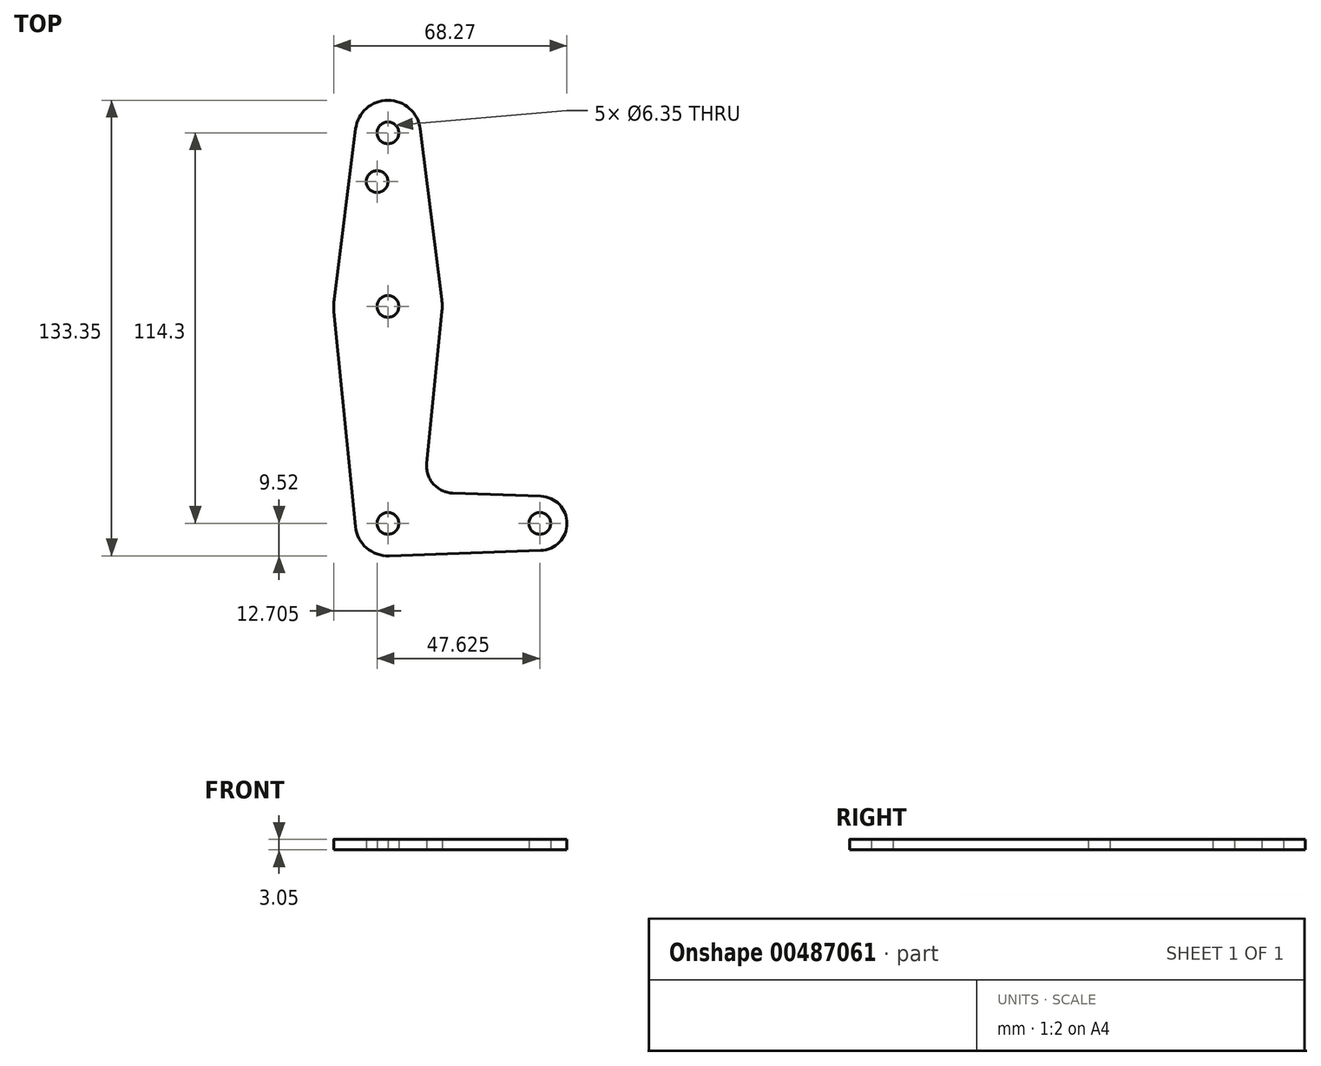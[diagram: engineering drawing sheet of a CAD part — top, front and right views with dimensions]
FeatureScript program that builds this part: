
annotation { "Feature Type Name" : "Feature", "Feature Type Description" : "" }
export const myFeature = defineFeature(function(context is Context, id is Id, definition is map)
    precondition{}
    {
        {
            var Q0;
            Q0=qCreatedBy(makeId("Top.planeOp"),FACE);
            var sketch = newSketch(context, id + "F0", { "sketchPlane" : qUnion([Q0])});
            skLineSegment(sketch, "E0", {"start": v(44.45, 0) * mm, "end": v(0, 0) * mm, "construction": true});
            skCircle(sketch, "E1", {"center": v(0, 0) * mm, "radius": 9.53 * mm});
            skCircle(sketch, "E2", {"center": v(44.45, 0) * mm, "radius": 7.94 * mm});
            skCircle(sketch, "E3", {"center": v(0, 114.3) * mm, "radius": 9.53 * mm});
            skCircle(sketch, "E4", {"center": v(0, 63.5) * mm, "radius": 15.88 * mm});
            skLineSegment(sketch, "E5", {"start": v(0, 0) * mm, "end": v(0, 114.3) * mm, "construction": true});
            skLineSegment(sketch, "E6", {"start": v(9.45, 115.5) * mm, "end": v(15.75, 65.48) * mm});
            skLineSegment(sketch, "E7", {"start": v(-9.45, 115.5) * mm, "end": v(-15.75, 65.48) * mm});
            skLineSegment(sketch, "E8", {"start": v(15.8, 61.91) * mm, "end": v(11.34, 17.6) * mm});
            skLineSegment(sketch, "E9", {"start": v(-15.8, 61.91) * mm, "end": v(-9.48, -0.95) * mm});
            skLineSegment(sketch, "E10", {"start": v(18.97, 8.85) * mm, "end": v(44.73, 7.93) * mm});
            skLineSegment(sketch, "E11", {"start": v(0.34, -9.52) * mm, "end": v(44.73, -7.93) * mm});
            skCircle(sketch, "E12", {"center": v(0, 114.3) * mm, "radius": 3.18 * mm});
            skCircle(sketch, "E13", {"center": v(-3.18, 100.03) * mm, "radius": 3.18 * mm});
            skCircle(sketch, "E14", {"center": v(0, 63.5) * mm, "radius": 3.18 * mm});
            skCircle(sketch, "E15", {"center": v(0, 0) * mm, "radius": 3.18 * mm});
            skCircle(sketch, "E16", {"center": v(44.45, 0) * mm, "radius": 3.18 * mm});
            skArc(sketch, "E17.filletArc", {"start": v(11.34, 17.6) * mm, "mid": v(13.26, 11.57) * mm, "end": v(18.97, 8.85) * mm});
            skSolve(sketch);
        }
        {
            var Q0;
            Q0=makeQuery(id+"F0.imprint","IMPRINT",FACE,{"disambiguationData":[TD([[makeQuery(id+"F0.imprint","IMPRINT",EDGE,{"derivedFrom":sQuery(id+"F0.wireOp",EDGE,"E12")}),-1.0]])]});
            var Q1;
            {var subQ1=sQuery(id+"F0.wireOp",EDGE,"E6");Q1=makeQuery(id+"F0.imprint","IMPRINT",FACE,{"disambiguationData":[TD([[makeQuery(id+"F0.imprint","IMPRINT",EDGE,{"derivedFrom":subQ1}),-1.0]])]});}
            var Q2;
            Q2=makeQuery(id+"F0.imprint","IMPRINT",FACE,{"disambiguationData":[TD([[makeQuery(id+"F0.imprint","IMPRINT",EDGE,{"derivedFrom":sQuery(id+"F0.wireOp",EDGE,"E14")}),-1.0]])]});
            var Q3;
            {var subQ0=sQuery(id+"F0.wireOp",EDGE,"E8");Q3=makeQuery(id+"F0.imprint","IMPRINT",FACE,{"disambiguationData":[TD([[makeQuery(id+"F0.imprint","IMPRINT",EDGE,{"derivedFrom":subQ0}),-1.0]])]});}
            var Q4;
            Q4=makeQuery(id+"F0.imprint","IMPRINT",FACE,{"disambiguationData":[TD([[makeQuery(id+"F0.imprint","IMPRINT",EDGE,{"derivedFrom":sQuery(id+"F0.wireOp",EDGE,"E15")}),-1.0]])]});
            var Q5;
            Q5=makeQuery(id+"F0.imprint","IMPRINT",FACE,{"disambiguationData":[TD([[makeQuery(id+"F0.imprint","IMPRINT",EDGE,{"derivedFrom":sQuery(id+"F0.wireOp",EDGE,"E16")}),-1.0]])]});
            extrude(context, id + "F1", {"entities" : qUnion([Q0, Q1, Q2, Q3, Q4, Q5]), "depth" : 3.05 * mm});
        }
    });
